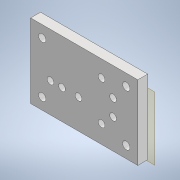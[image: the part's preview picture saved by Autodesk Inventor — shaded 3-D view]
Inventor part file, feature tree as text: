
AUTODESK INVENTOR PART (.ipt)
format: ipt  version: 2021 (Build 250183000, 183)  size: 175,616 bytes
history: native  units: in
note: dims shown in document units (in); Inventor stores cm internally (conversion verified against a paired STEP export)
features: reference x16, other x9, extrude x3, hole x3, sketch x3, plane x1, projected_geometry x1
ambient origin geometry x8: Origin, YZ Plane, XZ Plane, XY Plane, X Axis, Y Axis, Z Axis, Center Point
bodies: Solid1 (feature_tree)
feature tree (36):
  extrude  "Extrusion base plate"  [1 undecoded]
  plane  "work plane for rib creation"
  other  "channels as rib"
  extrude  "extrusion of ribs to get cutout"  Depth=0.2756in
  extrude  "valve space extrusion"  Depth=0.2362in TaperAngle=0.0deg
  other  "all valve spaces"
  hole  "holes for control layer"  [1 undecoded]
  hole  "holes for connection to flow layer"  [1 undecoded]
  hole  "holes in corners"  [1 undecoded]
  sketch  "Sketch1"  dims[d0=0.2362in d1=0.0in d2=-0.0394in]
  reference  "Reference1"
  reference  "Reference2"
  reference  "Reference3"
  reference  "Reference4"
  other  "channels and points for valves and for connectors for control layer"
  reference  "Reference5"
  reference  "Reference6"
  reference  "Reference7"
  reference  "Reference8"
  reference  "Reference9"
  reference  "Reference10"
  reference  "Reference11"
  sketch  "Sketch3"  dims[d3=0.2756in d4=0.2756in]
  projected_geometry  "Projected Loop1"
  sketch  "Sketch4"  dims[d11=0.0394in d12=0.0394in d13=0.0in d14=0.0in d15=0.0394in d16=0.0in d17=0.1024in d18=0.0in d19=0.1181in d20=0.0886in d21=0.063in d22=0.0in d23=0.1614in d24=0.2362in d25=0.1575in d26=0.0787in d27=90.0deg d28=0.0394in d29=0.0in d30=0.1614in d31=0.2362in d32=0.1575in d33=0.0787in d34=90.0deg d35=0.2106in d36=0.0in d37=0.1772in d38=0.2362in d39=0.1575in d40=0.0787in d41=90.0deg d42=0.4144in d43=0.0in]
  reference  "Reference12"
  other  "projected points for every valve"
  other  "projected points for every hole for control layer only"
  other  "projected points for every hole for flow layer only"
  other  "prohected points for corner holes"
  reference  "Reference13"
  reference  "Reference14"
  reference  "Reference15"
  reference  "Reference16"
  other  "Prototype Assembly.iam"
  other  "Prototype Flow Layer:1"
note: 4 required parameter values undecoded (feature->parameter linkage not recoverable at this tier; creation-order binding heuristic only, values carry confidence <= 0.55)
